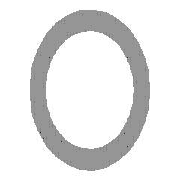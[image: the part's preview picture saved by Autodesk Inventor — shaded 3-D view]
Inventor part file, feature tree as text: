
AUTODESK INVENTOR PART (.ipt)
format: ipt  version: 2021 (Build 250183000, 183)  size: 280,064 bytes
history: native  units: mm (DEFAULTED — no unit token found)
features: other x13, plane x5, sketch x3, sweep x1, extrude x1
ambient origin geometry x8: Origin, YZ Plane, XZ Plane, XY Plane, X Axis, Y Axis, Z Axis, Center Point
bodies: Solid1 (feature_tree)
feature tree (23):
  parser-record x1  (decoder bookkeeping rows leaked as tree rows — omitted from the tree; the rows remain in map.json)
  other  "Driven Length"
  other  "Plano inicial"
  other  "Plano final"
  other  "Trayectoria de barrido"
  plane  "Plano de trabajo de orientación"
  sweep  "Cuerpo"
  plane  "Plano de trabajo5"
  plane  "Plano de trabajo6"
  plane  "Plano de trabajo7"
  extrude  "Extrusión2"  Depth=739.165161mm
  other  "Combinar5"
  sketch  "Sketch3"  dims[d0=33.528mm d1=4.5466mm]
  plane  "Work Plane3"
  sketch  "Sketch4"  dims[d4=-0.0mm d5=739.165161mm]
  sketch  "Boceto5"  dims[d6=90.0deg d7=739.165161mm d8=0.0mm d9=0.0mm d26=0.12mm d27=0.0mm d164=5.0mm d165=0.0mm d166=5.0mm d167=0.0mm]
  other  "Sólido6"
  other  "Sup116"
  other  "Sup117"
  other  "Sólido41"
  other  "Sup115"
  other  "Superficie de contorno77"
  other  "Superficie de contorno78"
